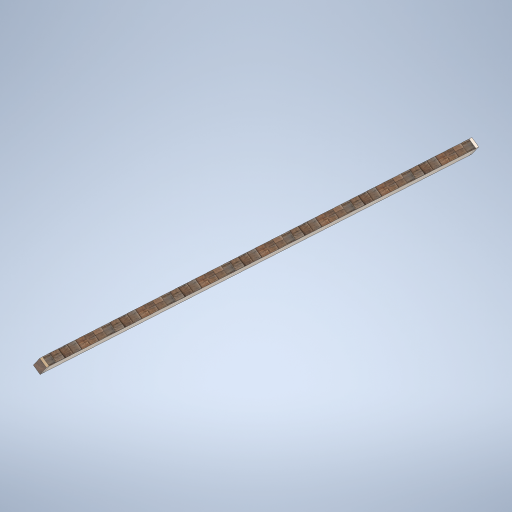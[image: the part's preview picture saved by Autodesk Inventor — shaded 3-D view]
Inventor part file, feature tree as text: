
AUTODESK INVENTOR PART (.ipt)
format: ipt  version: 2024.2 (Build 282272000, 272)  size: 307,712 bytes
history: native  units: mm
features: sketch x4, plane x2, extrude x2, projected_geometry x2, loft x1
ambient origin geometry x8: Origin, YZ Plane, XZ Plane, XY Plane, X Axis, Y Axis, Z Axis, Center Point
bodies: Solid1 (feature_tree)
feature tree (11):
  sketch  "Sketch1"  dims[d0=0.0mm d1=7900.0mm d2=0.0mm d3=90.0deg]
  plane  "Work Plane2"
  loft  "Loft1"
  sketch  "Sketch3"  dims[d8=50.0mm d9=0.0mm]
  sketch  "Sketch4"
  extrude  "Extrusion1"  Depth=50.0mm TaperAngle=0.0deg
  extrude  "Extrusion2"  [1 undecoded]
  plane  "Work Plane1"
  sketch  "Sketch2"  dims[d4=0.0mm d5=90.0deg d6=50.0mm d7=0.0mm]
  projected_geometry  "Projected Loop1"
  projected_geometry  "Projected Loop2"
note: 1 required parameter value undecoded (feature->parameter linkage not recoverable at this tier; creation-order binding heuristic only, values carry confidence <= 0.55)
